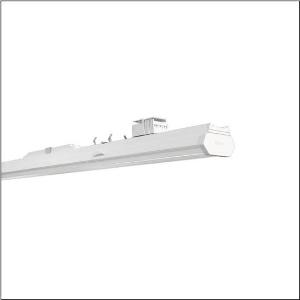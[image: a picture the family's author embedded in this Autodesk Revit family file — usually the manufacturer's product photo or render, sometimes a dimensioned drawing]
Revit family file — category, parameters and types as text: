
# Revit family: licross_r__11_protected_ho_51tp12dn4fxmd_e40f
name_source: partatom
category: Lighting Fixtures
units: mm (PartAtom-declared; Revit-internal decimal feet)

## family parameters
Cut with Voids When Loaded = No
Host = Face
Light Source = No
Part Type = Normal
Room Calculation Point = No
Round Connector Dimension = Use Diameter
Shared = No

## types (1)
- --- (1 x LED, 2290 lm, 13.9 W, 4000K)
    Apparent Load = 14 VA
    CIE Flux Codes = 70 91 97 98 100
    Color Rendering = 80
    Color Temperature = 4000K
    Default Elevation = 1800 mm
    Description = Licross® 11 Protected HO, luminaire insert, of sheet steel, galvanised, coil coated, white, length: 1.500mm, width: 90mm, height: 101mm, LED rated luminous flux: 15.270lm, light colour: 840, SDCM (Standard Deviation of Colour Matching)MacAdam ≤ 2 SDCM (initial), control gear: DALI 2 (for two DALI lines), with plug, 6-pole, with phase selection, mains connection: 220..240V, AC/DC, 0/50..60Hz, rated input power: 87W, internal wiring halogen-free, for central battery installations according to EN 60598-2-22, for emergency light function, without changeover relay, primary optical cover: cover, of PMMA, light emission: direct distribution, primary light characteristic: symmetric, protection rating (complete): IP64, insulation class (complete): insulation class I (protective earthing), certification: CE, ENEC, VDE, UKCA, protection symbol: D if used in an environment with conductive dust loads with corresponding accessories, impact resistance: IK06, permissible ambient temperature for indoor applications: -25..+30°C, standard: EN 60598-2-22, corresponds to IFS (International Featured Standards) requirements for safety and quality in the food industry, reducing of maximum allowable ambient temperature of 5°C with ceiling mounting, LABS conformity tested according to VDMA 24364:2018-05, packaging unit: 1 piece
    Height = 92 mm
    Lamp = 1 x LED
    Lamp Light Flux = 2290 lm
    Lamp Power = 13.9 W
    Lamp count = 1
    Length = 1500 mm
    Luminous efficacy = 165 lm/W
    Manufacturer = Siteco
    ModVariant = No
    Model = 51TP12DN4FXMD
    Mounting Place = Ceiling
    Mounting Type = Pendant
    Number of Poles = 1
    OnlyDefault = Yes
    Power Factor = 1
    Product Name = Licross® 11 Protected HO
    Product group = luminaire insert | ceiling pendant
    ProductGroupID = 901
    Protection Class = Protection class I
    Protection Degree = IP 64
    RLX_Detail_Level = 1
    RLX_Emergency_Light_Flux = 0 lm
    RLX_Emergency_Type = 0
    RLX_Emergency_Type_DB = No
    RlxData = <blob elided: 24833 chars, md5=1500206f>
    Socket = socket
    Standby Power = 0 W
    System Light Flux = 2290 lm
    System Power = 14 W
    Type Comments = : DC mode (central or group accumulator) initial emergency light level
    Type Image = l_1256148.jpg
    URL = http://relux.com
    VarID = @adj_095409
    Voltage = 0 V
    Weight = 0.00 kg
    Width = 88 mm

## geometry (parser evidence)
native form markers: Blend x4, Sweep x9
no freeform markers — native parametric forms only
